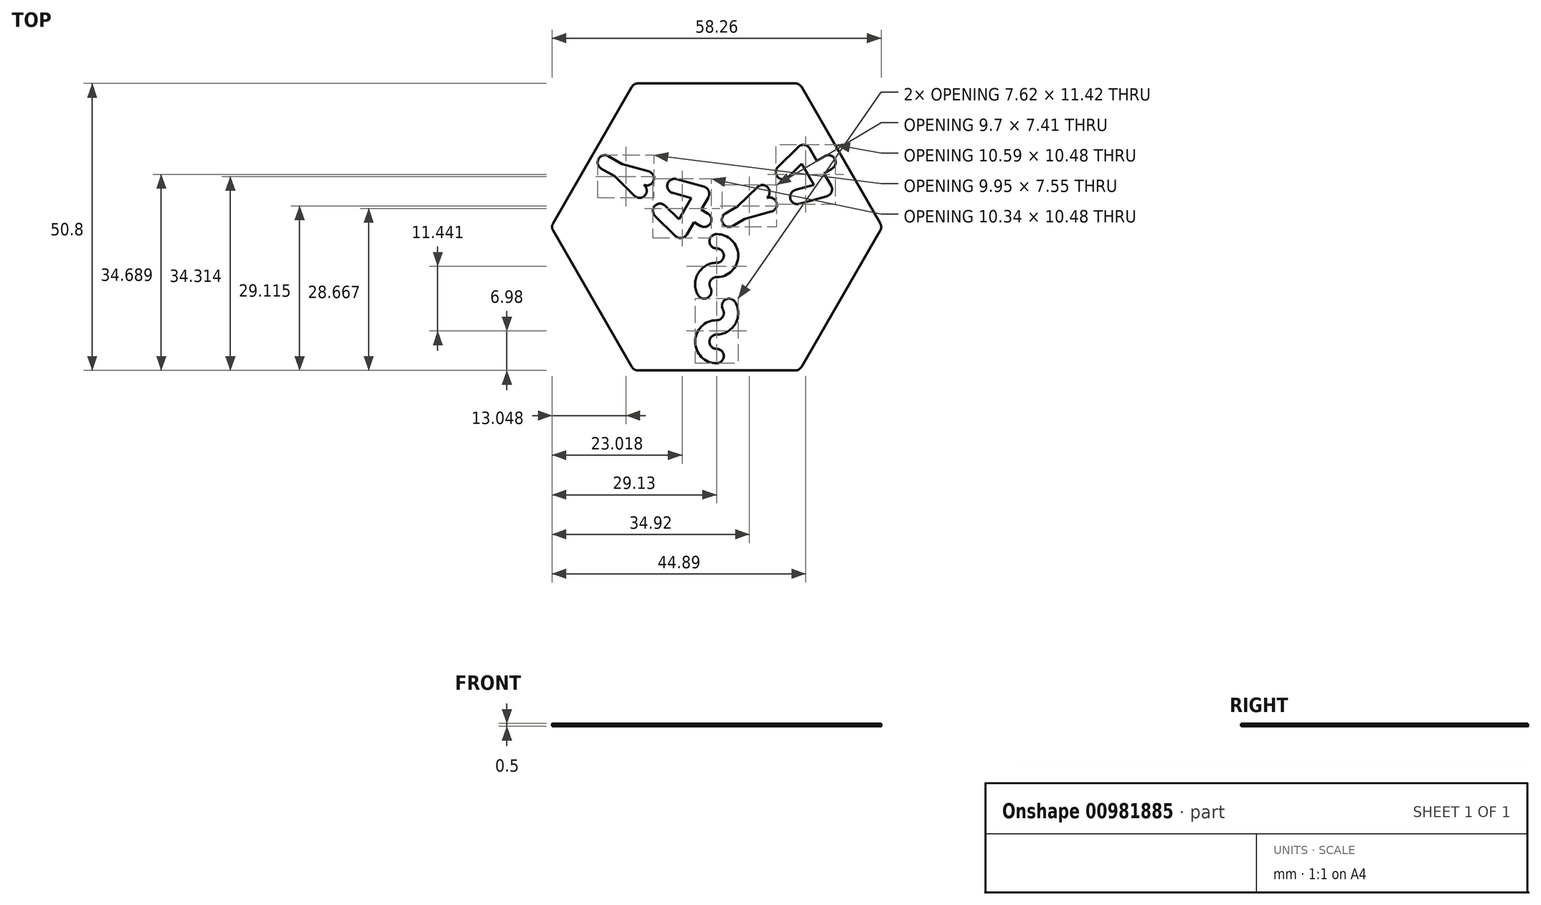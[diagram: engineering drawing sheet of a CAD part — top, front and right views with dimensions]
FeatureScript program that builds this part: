
annotation { "Feature Type Name" : "Feature", "Feature Type Description" : "" }
export const myFeature = defineFeature(function(context is Context, id is Id, definition is map)
    precondition{}
    {
        {
            var Q0;
            Q0=qCreatedBy(makeId("Top.planeOp"),FACE);
            var sketch = newSketch(context, id + "F0", { "sketchPlane" : qUnion([Q0]), "disableImprinting" : false});
            skCircle(sketch, "E0.cCircle", {"center": v(0, 0) * mm, "radius": 25.4 * mm, "construction": true});
            skLineSegment(sketch, "E0.0", {"start": v(14.66, -25.4) * mm, "end": v(-14.66, -25.4) * mm});
            skLineSegment(sketch, "E0.1", {"start": v(-14.66, -25.4) * mm, "end": v(-29.33, 0) * mm});
            skLineSegment(sketch, "E0.2", {"start": v(-29.33, 0) * mm, "end": v(-14.66, 25.4) * mm});
            skLineSegment(sketch, "E0.3", {"start": v(-14.66, 25.4) * mm, "end": v(14.66, 25.4) * mm});
            skLineSegment(sketch, "E0.4", {"start": v(14.66, 25.4) * mm, "end": v(29.33, 0) * mm});
            skLineSegment(sketch, "E0.5", {"start": v(29.33, 0) * mm, "end": v(14.66, -25.4) * mm});
            skPoint(sketch, "E0.0.midPoint", {"position": v(0, -25.4) * mm});
            skLineSegment(sketch, "E1", {"start": v(-2.2, 1.27) * mm, "end": v(-3.38, 1.95) * mm, "construction": true});
            skLineSegment(sketch, "E2", {"start": v(19.8, 11.43) * mm, "end": v(2.2, 1.27) * mm, "construction": true});
            skPoint(sketch, "E3.endSnap0", {"position": v(17.26, 9.97) * mm});
            skLineSegment(sketch, "E4", {"start": v(15.36, 13.27) * mm, "end": v(19.17, 6.67) * mm, "construction": true});
            skLineSegment(sketch, "E5", {"start": v(-17.26, 9.97) * mm, "end": v(-12.37, 8.6) * mm, "construction": true});
            skLineSegment(sketch, "E6", {"start": v(-2.58, 5.89) * mm, "end": v(-6.39, -0.71) * mm, "construction": true});
            skPoint(sketch, "E7", {"position": v(-4.48, 2.59) * mm});
            skLineSegment(sketch, "E8", {"start": v(15.36, 13.27) * mm, "end": v(4.48, 2.59) * mm, "construction": true});
            skLineSegment(sketch, "E9", {"start": v(4.48, 2.59) * mm, "end": v(9.38, 3.95) * mm, "construction": true});
            skArc(sketch, "E10", {"start": v(0, -2.54) * mm, "mid": v(2.54, -5.08) * mm, "end": v(0, -7.62) * mm, "construction": true});
            skArc(sketch, "E11", {"start": v(0, -7.62) * mm, "mid": v(-2.54, -10.16) * mm, "end": v(0, -12.7) * mm, "construction": true});
            skArc(sketch, "E12", {"start": v(0, -12.7) * mm, "mid": v(2.54, -15.24) * mm, "end": v(0, -17.78) * mm, "construction": true});
            skArc(sketch, "E13", {"start": v(0, -17.78) * mm, "mid": v(-2.54, -20.32) * mm, "end": v(0, -22.86) * mm, "construction": true});
            skCircle(sketch, "E14", {"center": v(0, 0) * mm, "radius": 2.54 * mm, "construction": true});
            skCircle(sketch, "E15", {"center": v(0, 0) * mm, "radius": 22.86 * mm, "construction": true});
            skArc(sketch, "E16.4.startCap", {"start": v(19.16, 12.53) * mm, "mid": v(20.9, 12.07) * mm, "end": v(20.43, 10.33) * mm});
            skArc(sketch, "E16.4.endCap", {"start": v(2.83, 0.17) * mm, "mid": v(1.1, 0.64) * mm, "end": v(1.56, 2.37) * mm});
            skLineSegment(sketch, "E16.4.left", {"start": v(20.43, 10.33) * mm, "end": v(19, 9.5) * mm});
            skLineSegment(sketch, "E16.4.right", {"start": v(19.16, 12.53) * mm, "end": v(17.73, 11.7) * mm});
            skArc(sketch, "E16.5.startCap", {"start": v(-1.56, 2.37) * mm, "mid": v(-1.1, 0.64) * mm, "end": v(-2.83, 0.17) * mm});
            skArc(sketch, "E16.5.endCap", {"start": v(-20.43, 10.33) * mm, "mid": v(-20.9, 12.07) * mm, "end": v(-19.16, 12.53) * mm});
            skLineSegment(sketch, "E16.5.left", {"start": v(-2.83, 0.17) * mm, "end": v(-4.02, 0.85) * mm});
            skLineSegment(sketch, "E16.5.right", {"start": v(-1.56, 2.37) * mm, "end": v(-2.75, 3.05) * mm});
            skArc(sketch, "E17.0.startCap", {"start": v(0, -3.8) * mm, "mid": v(-1.27, -2.54) * mm, "end": v(0, -1.27) * mm});
            skArc(sketch, "E17.0.left", {"start": v(0, -1.27) * mm, "mid": v(3.81, -5.08) * mm, "end": v(0, -8.89) * mm});
            skArc(sketch, "E17.0.right", {"start": v(0, -3.8) * mm, "mid": v(1.27, -5.08) * mm, "end": v(0, -6.35) * mm});
            skArc(sketch, "E17.1.left", {"start": v(0, -8.89) * mm, "mid": v(-1.1, -9.52) * mm, "end": v(-1.1, -10.8) * mm});
            skArc(sketch, "E17.1.right", {"start": v(0, -6.35) * mm, "mid": v(-3.3, -8.25) * mm, "end": v(-3.3, -12.06) * mm});
            skArc(sketch, "E17.2.left", {"start": v(0, -11.43) * mm, "mid": v(1.9, -11.94) * mm, "end": v(3.3, -13.34) * mm, "construction": true});
            skArc(sketch, "E17.2.right", {"start": v(0.4, -14.04) * mm, "mid": v(0.8, -14.26) * mm, "end": v(1.1, -14.6) * mm, "construction": true});
            skArc(sketch, "E17.3.endCap", {"start": v(0, -21.6) * mm, "mid": v(1.27, -22.86) * mm, "end": v(0, -24.13) * mm});
            skArc(sketch, "E17.3.left", {"start": v(0, -19.05) * mm, "mid": v(-1.27, -20.32) * mm, "end": v(0, -21.6) * mm});
            skArc(sketch, "E17.3.right", {"start": v(0, -16.51) * mm, "mid": v(-3.81, -20.32) * mm, "end": v(0, -24.13) * mm});
            skCircle(sketch, "E18", {"center": v(0, 0) * mm, "radius": 12.7 * mm, "construction": true});
            skArc(sketch, "E19.0.startCap", {"start": v(20.27, 7.3) * mm, "mid": v(20.34, 6.19) * mm, "end": v(19.5, 5.44) * mm});
            skArc(sketch, "E19.0.endCap", {"start": v(14.47, 14.17) * mm, "mid": v(15.53, 14.53) * mm, "end": v(16.46, 13.9) * mm});
            skLineSegment(sketch, "E19.0.right", {"start": v(19, 9.5) * mm, "end": v(20.27, 7.3) * mm});
            skLineSegment(sketch, "E20", {"start": v(14.27, 5.3) * mm, "end": v(19.17, 6.67) * mm, "construction": true});
            skLineSegment(sketch, "E21", {"start": v(9.38, 3.95) * mm, "end": v(14.27, 5.3) * mm, "construction": true});
            skArc(sketch, "E22.0.startCap", {"start": v(14.61, 4.08) * mm, "mid": v(13.05, 4.97) * mm, "end": v(13.93, 6.53) * mm});
            skLineSegment(sketch, "E22.0.left", {"start": v(13.93, 6.53) * mm, "end": v(17.25, 7.45) * mm});
            skLineSegment(sketch, "E22.0.right", {"start": v(14.61, 4.08) * mm, "end": v(19.5, 5.44) * mm});
            skArc(sketch, "E22.1.endCap", {"start": v(9.04, 5.17) * mm, "mid": v(10.6, 4.29) * mm, "end": v(9.72, 2.72) * mm});
            skLineSegment(sketch, "E22.1.right", {"start": v(4.98, 1.4) * mm, "end": v(9.72, 2.72) * mm});
            skLineSegment(sketch, "E23.trimOffspring", {"start": v(3.7, 3.6) * mm, "end": v(1.56, 2.37) * mm});
            skLineSegment(sketch, "E24.MirrorCS", {"start": v(12.62, 8.8) * mm, "end": v(15.08, 11.21) * mm});
            skArc(sketch, "E25.MirrorCS", {"start": v(10.84, 10.61) * mm, "mid": v(10.83, 8.82) * mm, "end": v(12.62, 8.8) * mm});
            skLineSegment(sketch, "E26.MirrorCS", {"start": v(10.84, 10.61) * mm, "end": v(14.47, 14.17) * mm});
            skLineSegment(sketch, "E27.MirrorCS", {"start": v(3.7, 3.6) * mm, "end": v(7.22, 7.05) * mm});
            skArc(sketch, "E28.MirrorCS", {"start": v(9, 5.24) * mm, "mid": v(9.02, 7.04) * mm, "end": v(7.22, 7.05) * mm});
            skLineSegment(sketch, "E29.MirrorCS", {"start": v(8.88, 5.13) * mm, "end": v(9, 5.24) * mm});
            skLineSegment(sketch, "E30.trimOffspring", {"start": v(4.98, 1.4) * mm, "end": v(2.83, 0.17) * mm});
            skLineSegment(sketch, "E31.trimOffspring", {"start": v(8.88, 5.13) * mm, "end": v(9.04, 5.17) * mm});
            skLineSegment(sketch, "E32.trimOffspring", {"start": v(15.08, 11.21) * mm, "end": v(17.25, 7.45) * mm});
            skLineSegment(sketch, "E33.trimOffspring", {"start": v(16.46, 13.9) * mm, "end": v(17.73, 11.7) * mm});
            skArc(sketch, "E34", {"start": v(-1.1, -10.8) * mm, "mid": v(-1.56, -12.53) * mm, "end": v(-3.3, -12.06) * mm});
            skArc(sketch, "E35", {"start": v(3.3, -13.34) * mm, "mid": v(1.56, -12.87) * mm, "end": v(1.1, -14.6) * mm});
            skCircle(sketch, "E36", {"center": v(0, -12.7) * mm, "radius": 1.27 * mm, "construction": true});
            skArc(sketch, "E37", {"start": v(3.3, -13.34) * mm, "mid": v(3.3, -17.15) * mm, "end": v(0, -19.05) * mm});
            skArc(sketch, "E38", {"start": v(-1.1, -10.8) * mm, "mid": v(-0.64, -11.26) * mm, "end": v(0, -11.43) * mm, "construction": true});
            skArc(sketch, "E39", {"start": v(-3.3, -12.06) * mm, "mid": v(-2.24, -13.24) * mm, "end": v(-0.8, -13.88) * mm, "construction": true});
            skArc(sketch, "E40", {"start": v(1.1, -14.6) * mm, "mid": v(1.1, -15.88) * mm, "end": v(0, -16.51) * mm});
            skLineSegment(sketch, "E41.trimOffspring", {"start": v(-16.77, 11.15) * mm, "end": v(-19.16, 12.53) * mm});
            skLineSegment(sketch, "E42.trimOffspring", {"start": v(-18.04, 8.95) * mm, "end": v(-20.43, 10.33) * mm});
            skPoint(sketch, "E43.trimOffspring.start.orphan", {"position": v(-17.26, 9.97) * mm});
            skLineSegment(sketch, "E44", {"start": v(-12.37, 8.6) * mm, "end": v(-7.47, 7.25) * mm, "construction": true});
            skLineSegment(sketch, "E45", {"start": v(-7.47, 7.25) * mm, "end": v(-2.58, 5.89) * mm, "construction": true});
            skArc(sketch, "E46.0.startCap", {"start": v(-2.24, 7.11) * mm, "mid": v(-1.4, 6.37) * mm, "end": v(-1.48, 5.25) * mm});
            skArc(sketch, "E46.0.endCap", {"start": v(-5.29, -1.35) * mm, "mid": v(-6.22, -1.97) * mm, "end": v(-7.28, -1.62) * mm});
            skLineSegment(sketch, "E46.0.left", {"start": v(-1.48, 5.25) * mm, "end": v(-2.75, 3.05) * mm});
            skArc(sketch, "E46.1.startCap", {"start": v(-7.81, 6.02) * mm, "mid": v(-8.7, 7.59) * mm, "end": v(-7.13, 8.47) * mm});
            skArc(sketch, "E46.1.endCap", {"start": v(-2.24, 7.11) * mm, "mid": v(-1.4, 6.37) * mm, "end": v(-1.48, 5.25) * mm});
            skLineSegment(sketch, "E46.1.left", {"start": v(-7.13, 8.47) * mm, "end": v(-2.24, 7.11) * mm});
            skLineSegment(sketch, "E46.1.right", {"start": v(-7.81, 6.02) * mm, "end": v(-4.5, 5.1) * mm});
            skArc(sketch, "E46.2.endCap", {"start": v(-12.03, 9.83) * mm, "mid": v(-11.15, 8.27) * mm, "end": v(-12.7, 7.38) * mm});
            skLineSegment(sketch, "E46.2.left", {"start": v(-16.77, 11.15) * mm, "end": v(-12.03, 9.83) * mm});
            skLineSegment(sketch, "E46.2.right", {"start": v(-12.86, 7.43) * mm, "end": v(-12.7, 7.38) * mm});
            skLineSegment(sketch, "E47.MirrorCS", {"start": v(-9.12, 3.75) * mm, "end": v(-6.67, 1.34) * mm});
            skArc(sketch, "E48.MirrorCS", {"start": v(-9.12, 3.75) * mm, "mid": v(-10.92, 3.74) * mm, "end": v(-10.9, 1.94) * mm});
            skLineSegment(sketch, "E49.MirrorCS", {"start": v(-10.9, 1.94) * mm, "end": v(-7.28, -1.62) * mm});
            skLineSegment(sketch, "E50.MirrorCS", {"start": v(-18.04, 8.95) * mm, "end": v(-14.53, 5.5) * mm});
            skArc(sketch, "E51.MirrorCS", {"start": v(-14.53, 5.5) * mm, "mid": v(-12.73, 5.52) * mm, "end": v(-12.75, 7.31) * mm});
            skLineSegment(sketch, "E52.trimOffspring", {"start": v(-4.02, 0.85) * mm, "end": v(-5.29, -1.35) * mm});
            skLineSegment(sketch, "E53.trimOffspring", {"start": v(-12.86, 7.43) * mm, "end": v(-12.75, 7.31) * mm});
            skLineSegment(sketch, "E54.trimOffspring", {"start": v(-4.5, 5.1) * mm, "end": v(-6.67, 1.34) * mm});
            skCircle(sketch, "E55", {"center": v(11.83, 4.63) * mm, "radius": 1.27 * mm, "construction": true});
            skCircle(sketch, "E56", {"center": v(-9.92, 7.93) * mm, "radius": 1.27 * mm, "construction": true});
            skArc(sketch, "E57", {"start": v(22.63, 11.6) * mm, "mid": v(20.9, 12.05) * mm, "end": v(21.33, 13.78) * mm, "construction": true});
            skSolve(sketch);
        }
        {
            assignVariable(context, id + "F1", {"name" : "thk", "anyValue" : .497});
        }
        {
            var Q0;
            Q0 = qSketchRegion(id + "F0", true);
            extrude(context, id + "F2", {"entities" : qUnion([Q0]), "flatOperationType" : FlatOperationType.REMOVE, "depth" : (getVariable(context, 'thk')) * mm, "offsetDistance" : 25.4 * mm, "startOffsetBound" : StartOffsetType.BLIND, "startOffsetDistance" : 25.4 * mm, "symmetric" : true, "domain" : OperationDomain.MODEL});
        }
        {
            var Q0;
            Q0=makeQuery(id+"F2.opExtrude","SWEPT_EDGE",EDGE,{"disambiguationData":[OSD([sQuery(id+"F0.wireOp",EDGE,"E0.1"),sQuery(id+"F0.wireOp",EDGE,"E0.2")])]});
            var Q1;
            Q1=makeQuery(id+"F2.opExtrude","SWEPT_EDGE",EDGE,{"disambiguationData":[OSD([sQuery(id+"F0.wireOp",EDGE,"E0.0"),sQuery(id+"F0.wireOp",EDGE,"E0.1")])]});
            var Q2;
            Q2=makeQuery(id+"F2.opExtrude","SWEPT_EDGE",EDGE,{"disambiguationData":[OSD([sQuery(id+"F0.wireOp",EDGE,"E0.0"),sQuery(id+"F0.wireOp",EDGE,"E0.5")])]});
            var Q3;
            Q3=makeQuery(id+"F2.opExtrude","SWEPT_EDGE",EDGE,{"disambiguationData":[OSD([sQuery(id+"F0.wireOp",EDGE,"E0.4"),sQuery(id+"F0.wireOp",EDGE,"E0.5")])]});
            var Q4;
            Q4=makeQuery(id+"F2.opExtrude","SWEPT_EDGE",EDGE,{"disambiguationData":[OSD([sQuery(id+"F0.wireOp",EDGE,"E0.3"),sQuery(id+"F0.wireOp",EDGE,"E0.4")])]});
            var Q5;
            Q5=makeQuery(id+"F2.opExtrude","SWEPT_EDGE",EDGE,{"disambiguationData":[OSD([sQuery(id+"F0.wireOp",EDGE,"E0.2"),sQuery(id+"F0.wireOp",EDGE,"E0.3")])]});
            fillet(context, id + "F3", {"entities" : qUnion([Q0, Q1, Q2, Q3, Q4, Q5]), "radius" : 1.27 * mm, "width" : 5.08 * mm, "tangentPropagation" : true, "blendControlType" : BlendControlType.RADIUS, "defaultsChanged" : false, "isAsymmetric" : false, "otherRadius" : 5.08 * mm, "flipAsymmetric" : false, "isPartial" : false, "partialFirstEdgeTotalParameter" : 0.01, "partialOppositeParameter" : true, "secondBound" : false, "partialSecondEdgeTotalParameter" : 0.99, "vertexSettings" : [], "pointOnEdgeSettings" : [], "allowEdgeOverflow" : false, "smoothCorners" : false, "filletType" : FilletType.EDGE});
        }
    });
